# Revit family: Lighting_Pendant_Nordlux_Nori-39-Pendant
name_source: partatom
category: Lighting Fixtures
revit_build: Autodesk Revit 2018 (Build: 20190510_1515(x64)
units: mm (PartAtom-declared; Revit-internal decimal feet)

## family parameters
Cut with Voids When Loaded = No
Host = Face
Light Source = Yes
OmniClass Number = 23.35.47.11
OmniClass Title = Lighting Fixtures
Part Type = Normal
Room Calculation Point = No
Round Connector Dimension = Use Diameter
Shared = No

## types (4) — shared parameters
Apparent Load = 7 VA
BIMobject category = Pendant
Beam angle = 153.80°
Body material = Nordlux  - Wood  - Dark wood
CQS = 80.9
CRI / Ra = 80.7
Color Filter = 16777215
Default Elevation = 1219 mm
Description = Nordic minimalism and suspended lightness are the keywords for the Nori pendant series by Danish designers Bjørn + Balle.
Design country = Denmark
Dimming Lamp Color Temperature Shift = <None>
Edition number = 1
Flicker frequency = 99 Hz
IFC Classification = Light Fixture
Installation instructions = https://asset.productmarketingcloud.com
Light bulb material = Nordlux  - Glass  - Glass transparent
Light bulb thread material = Nordlux  - Metal  - Black
Manufacturer = Nordlux
Manufacturer country = China
Manufacturer name = Nordlux
Material main = Metal
Material secondary = Wood
Model = Nori 39
NominalVoltage = 230 V
OmniClass Code = 23-35 47 11
OmniClass Description = Lighting Fixtures
Peak [cd] = 151
Photometric Web File = Nori 39 Pendant Br. Steel.ies
Power factor = 0.53
Product Guid = a5291f3c-762c-431b-887c-ea44bb711c51
Product SKU = Nori-39-Pendant
Product data url = https://bimobject.com
Product family = Lighting
Product group = Pendant
Product name = Nori 39 Pendant
Product url = https://nordlux.com
QR code = https://bimobject.com
TM30 Rf = 84.7
TM30 Rg = 94.4
Tilt Angle = 0.00°
URL = www.nordlux.com
Weight Net (Kg) = 1,2
Youtube clip = https://www.youtube.com

## per-type parameters (varying)
| type | Cord material | EANNumber | Shade inner material | Shade material | Upper body material |
| ART - (2120823001) Finish colour - (White) | Nordlux  - Metal  - White RAL 9016 | 2120823001 | Nordlux  - Metal  - White RAL 9016 | Nordlux  - Metal  - White RAL 9016 | Nordlux  - Metal  - White RAL 9016 |
| ART - (2120823003) Finish colour - (Black) | Nordlux  - Metal  - Black | 2120823003 | Nordlux  - Metal  - White RAL 9016 | Nordlux  - Metal  - Black | Nordlux  - Metal  - Black |
| ART - (2120823030) Finish colour - (Copper) | Nordlux  - Metal  - Black | 2120823030 | Nordlux  - Metal  - Copper | Nordlux  - Metal  - Copper | Nordlux  - Metal  - Black |
| ART - (2120823032) Finish colour - (Brushed steel) | Nordlux  - Metal  - Black | 2120823032 | Nordlux  - Metal  - Brushed steel | Nordlux  - Metal  - Brushed steel | Nordlux  - Metal  - Black |

## geometry (parser evidence)
native form markers: Sweep x4
no freeform markers — native parametric forms only
